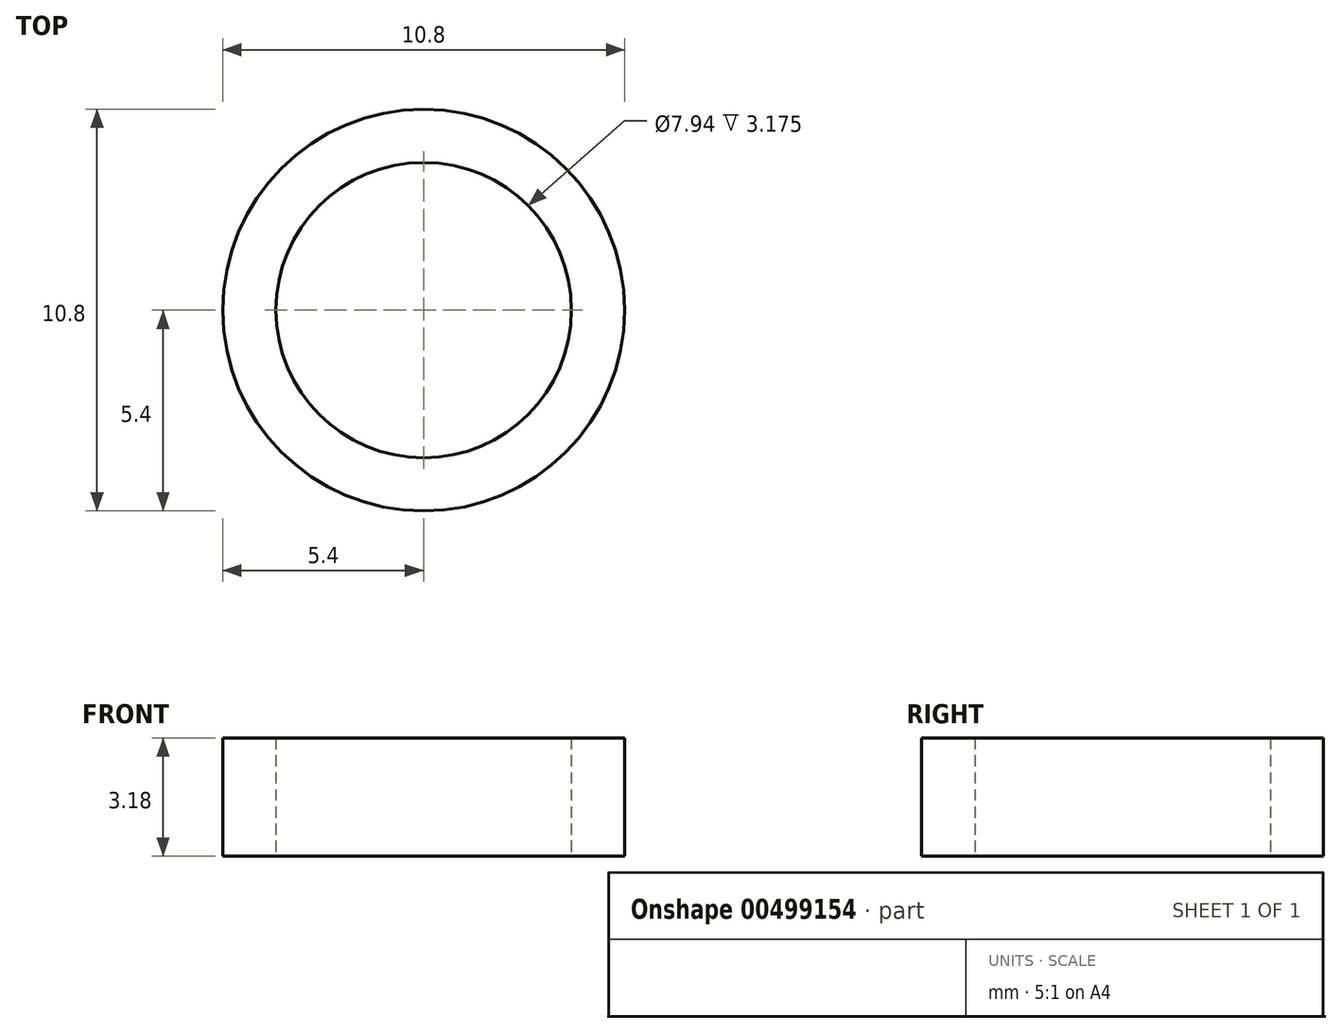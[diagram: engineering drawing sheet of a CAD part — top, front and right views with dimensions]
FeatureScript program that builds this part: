
annotation { "Feature Type Name" : "Feature", "Feature Type Description" : "" }
export const myFeature = defineFeature(function(context is Context, id is Id, definition is map)
    precondition{}
    {
        {
            var Q0;
            Q0=qCreatedBy(makeId("Top.planeOp"),FACE);
            var sketch = newSketch(context, id + "F0", { "sketchPlane" : qUnion([Q0])});
            skCircle(sketch, "E0", {"center": v(0, 0) * mm, "radius": 3.97 * mm});
            skCircle(sketch, "E1", {"center": v(0, 0) * mm, "radius": 5.4 * mm});
            skSolve(sketch);
        }
        {
            var Q0;
            Q0=makeQuery(id+"F0.imprint","IMPRINT",FACE,{"disambiguationData":[TD([[makeQuery(id+"F0.imprint","IMPRINT",EDGE,{"derivedFrom":sQuery(id+"F0.wireOp",EDGE,"E0")}),-1.0]])]});
            extrude(context, id + "F1", {"entities" : qUnion([Q0]), "depth" : 3.17 * mm});
        }
    });
